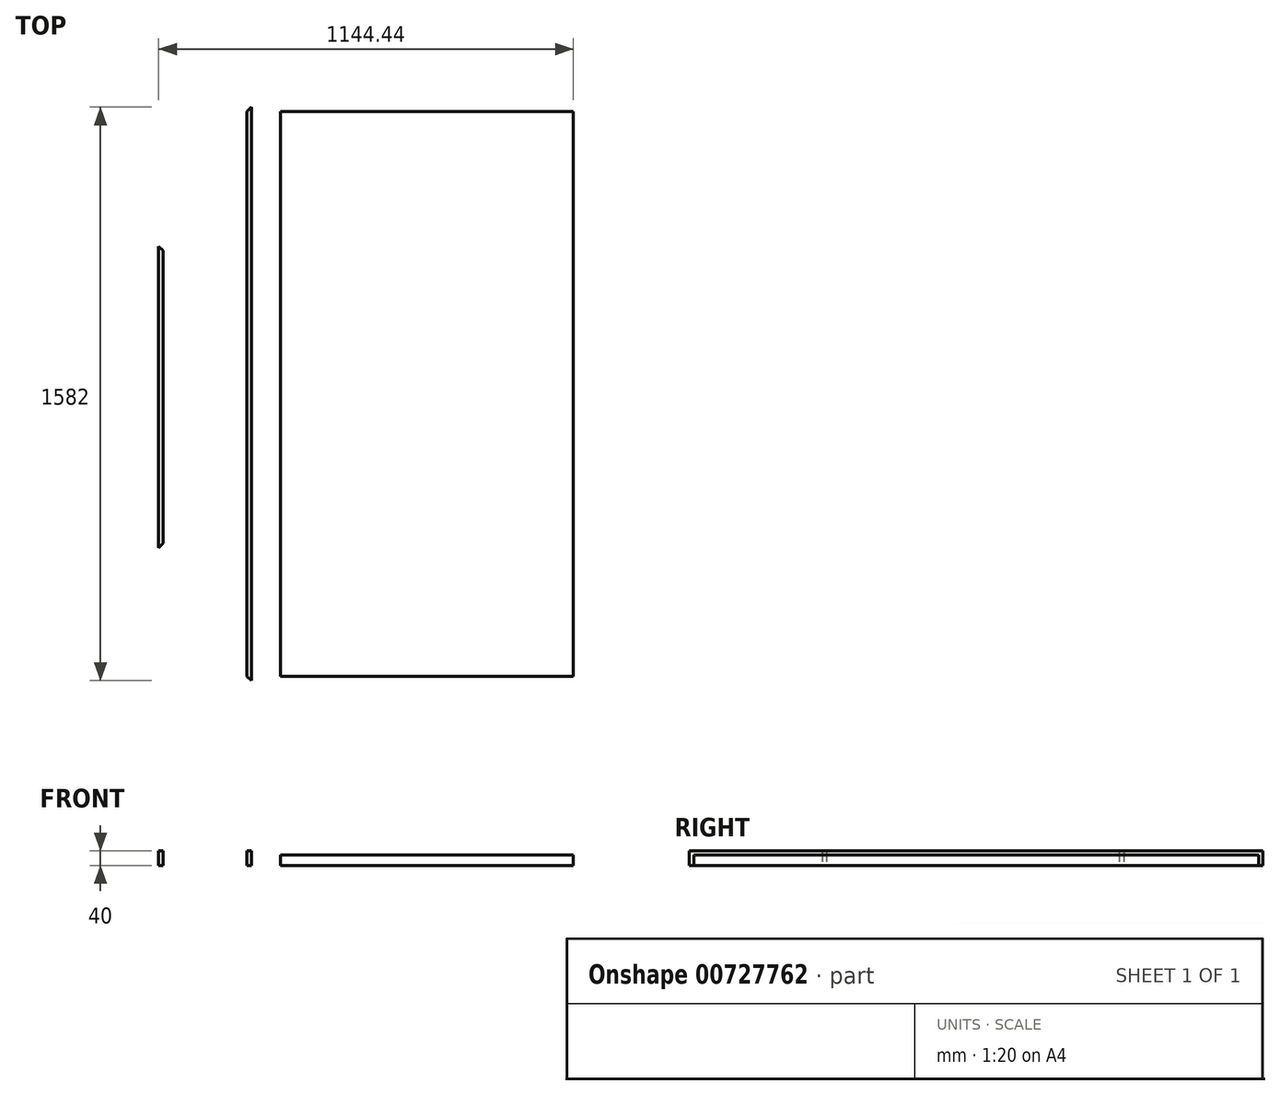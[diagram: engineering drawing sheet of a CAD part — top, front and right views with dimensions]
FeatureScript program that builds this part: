
annotation { "Feature Type Name" : "Feature", "Feature Type Description" : "" }
export const myFeature = defineFeature(function(context is Context, id is Id, definition is map)
    precondition{}
    {
        {
            var Q0;
            Q0=qCreatedBy(makeId("Top.planeOp"), FACE);
            var sketch = newSketch(context, id + "F0", { "sketchPlane" : qUnion([Q0])});
            skLineSegment(sketch, "E0.left", {"start": v(-140.44, -425) * mm, "end": v(-140.44, 407) * mm});
            skPoint(sketch, "E0.middle", {"position": v(-129.94, 0) * mm});
            skLineSegment(sketch, "E1", {"start": v(-140.44, 407) * mm, "end": v(-128.44, 395) * mm});
            skLineSegment(sketch, "E2", {"start": v(-140.44, -425) * mm, "end": v(-128.44, -413) * mm});
            skLineSegment(sketch, "E3", {"start": v(-128.44, 395) * mm, "end": v(-128.44, -413) * mm});
            skSolve(sketch);
        }
        {
            var Q0;
            Q0 = qSketchRegion(id + "F0", true);
            extrude(context, id + "F1", {"entities" : qUnion([Q0]), "depth" : 40 * mm, "offsetDistance" : 25 * mm});
        }
        {
            var Q0;
            Q0=qCreatedBy(makeId("Top.planeOp"), FACE);
            var sketch = newSketch(context, id + "F2", { "sketchPlane" : qUnion([Q0])});
            skLineSegment(sketch, "E4.right", {"start": v(115.58, -791) * mm, "end": v(115.58, 791) * mm});
            skPoint(sketch, "E4.middle", {"position": v(114.08, 0) * mm});
            skLineSegment(sketch, "E5", {"start": v(115.58, 791) * mm, "end": v(103.58, 779) * mm});
            skLineSegment(sketch, "E6", {"start": v(115.58, -791) * mm, "end": v(103.58, -779) * mm});
            skLineSegment(sketch, "E7", {"start": v(103.58, -779) * mm, "end": v(103.58, 779) * mm});
            skSolve(sketch);
        }
        {
            var Q0;
            Q0 = qSketchRegion(id + "F2", true);
            extrude(context, id + "F3", {"entities" : qUnion([Q0]), "depth" : 40 * mm, "offsetDistance" : 25 * mm});
        }
        {
            var Q0;
            Q0=qCreatedBy(makeId("Top.planeOp"), FACE);
            var sketch = newSketch(context, id + "F4", { "sketchPlane" : qUnion([Q0])});
            skLineSegment(sketch, "E8.bottom", {"start": v(196, -779) * mm, "end": v(1004, -779) * mm});
            skLineSegment(sketch, "E8.top", {"start": v(196, 779) * mm, "end": v(1004, 779) * mm});
            skLineSegment(sketch, "E8.left", {"start": v(196, -779) * mm, "end": v(196, 779) * mm});
            skLineSegment(sketch, "E8.right", {"start": v(1004, -779) * mm, "end": v(1004, 779) * mm});
            skPoint(sketch, "E8.middle", {"position": v(600, 0) * mm});
            skSolve(sketch);
        }
        {
            var Q0;
            Q0 = qSketchRegion(id + "F4", true);
            extrude(context, id + "F5", {"entities" : qUnion([Q0]), "depth" : 28 * mm, "offsetDistance" : 25 * mm});
        }
    });
